# Revit family: Electrical_Equipment-HCS-LX_Series
name_source: partatom
category: Electrical Equipment
revit_build: Autodesk Revit 2014 (Build: 20130308_1515(x64)
units: mm (PartAtom-declared; Revit-internal decimal feet)

## types (1)
- LX
    AC Input = 120VAC (100–240V), 50-60HZ(Line and Neutral Single Phase only)
    Apparent Load = 0.000 VA
    Assembly Code = D50
    Certifications = UL60950-1; TUV EN60950-1
    Connector Description 1 = Power Supply
    Connector Description 2 = Controls
    DC adjustment range = Rated output voltage: +/-10%
    Default Elevation = 48 "
    Description = LX Lighting Control Panel System
    Device Material = Hubbell - White
    Efficiency = 83%
    Frequency = 60 Hz
    Load Classification = Power
    Manufacturer = Hubbell Control Solutions
    Model = LX Power Supply
    Operating environment = -4° to 22°F (-20°to 50°C) @100% load,140° F (60° C) @ 80% load
    Output = 24V; 0–1.5A
    Overload protection = 105% to 160% constant current limiting; auto-recovery
    Overvoltage protection = Rated output voltage: 115% to 135%
    Power Factor = 1
    Product Documentation Link = https://hubbellcdn.com
    Product Page URL = https://www.hubbell.com
    Tolerance = +/-1%
    Type Comments = Electrical Equipment
    URL = https://www.hubbell.com
    Voltage = 120V
    Warranty = Five-year limited
    Withstand voltage = I/P-O/P:3KVAC

## geometry (parser evidence)
native form markers: Sweep x2
no freeform markers — native parametric forms only
